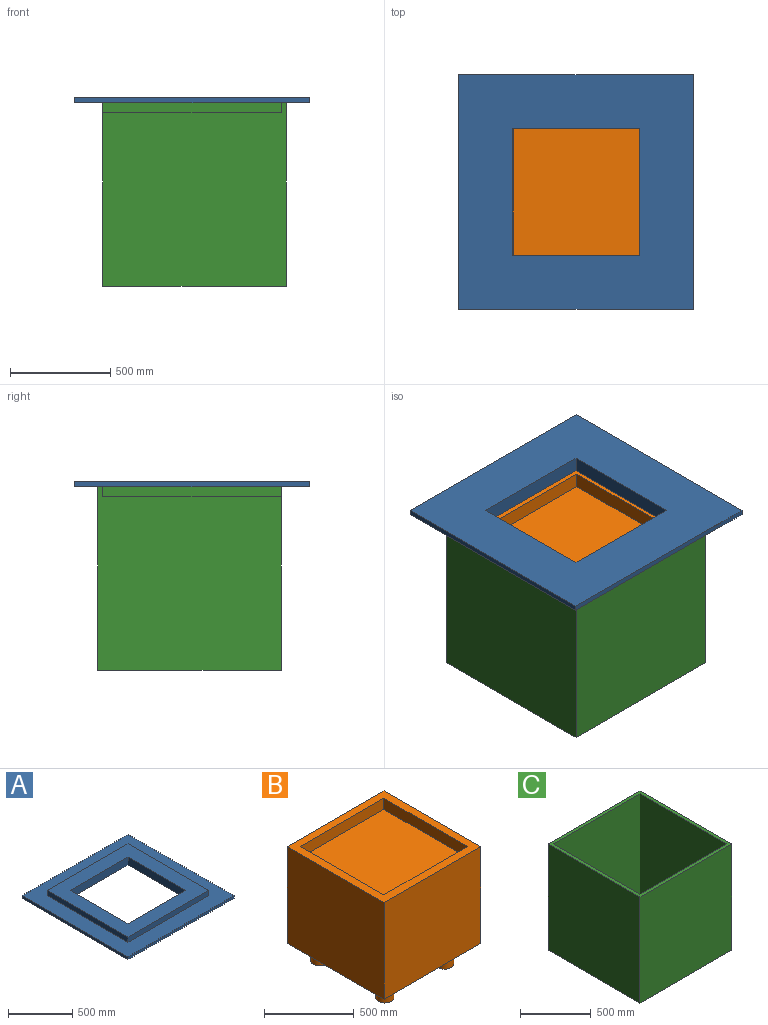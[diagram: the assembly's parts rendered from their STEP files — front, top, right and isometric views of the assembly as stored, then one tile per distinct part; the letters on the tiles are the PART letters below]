
ASSEMBLY  parts=3 mates=2
PART A: 15 faces, bbox 1168.4x1168.4x76.2 mm
  f0: plane 1168.4x1168.4mm, normal (0,0,-1), area 961933.6mm2, adj f3,f4,f5,f6,f11,f12,f13,f14
  f1: plane 889x889mm, normal (0,0,1), area 387096mm2, adj f7,f8,f9,f10,f11,f12,f13,f14
  f2: plane 1168.4x1168.4mm, normal (0,0,1), area 574837.6mm2, adj f3,f4,f5,f6,f7,f8,f9,f10
  f3: plane 1168.4x25.4mm, normal (1,0,0), area 29677.4mm2, adj f0,f2,f4,f6
  f4: plane 1168.4x25.4mm, normal (0,1,0), area 29677.4mm2, adj f0,f2,f3,f5
  f5: plane 1168.4x25.4mm, normal (-1,0,0), area 29677.4mm2, adj f0,f2,f4,f6
  f6: plane 1168.4x25.4mm, normal (0,-1,0), area 29677.4mm2, adj f0,f2,f3,f5
  f7: plane 889x50.8mm, normal (1,0,0), area 45161.2mm2, adj f1,f2,f8,f10
  f8: plane 889x50.8mm, normal (0,1,0), area 45161.2mm2, adj f1,f2,f7,f9
  f9: plane 889x50.8mm, normal (-1,0,0), area 45161.2mm2, adj f1,f2,f8,f10
  f10: plane 889x50.8mm, normal (0,-1,0), area 45161.2mm2, adj f1,f2,f7,f9
  f11: plane 635x76.2mm, normal (0,-1,0), area 48387mm2, adj f0,f1,f12,f13
  f12: plane 635x76.2mm, normal (1,0,0), area 48387mm2, adj f0,f1,f11,f14
  f13: plane 635x76.2mm, normal (-1,0,0), area 48387mm2, adj f0,f1,f11,f14
  f14: plane 635x76.2mm, normal (0,1,0), area 48387mm2, adj f0,f1,f12,f13
PART B: 19 faces, bbox 762x762x787.4 mm
  f0: plane 762x762mm, normal (0,0,1), area 144515.8mm2, adj f1,f2,f3,f4,f6,f7,f8,f9
  f1: plane 762x660.4mm, normal (0,1,0), area 503224.8mm2, adj f0,f2,f4,f5
  f2: plane 762x660.4mm, normal (-1,0,0), area 503224.8mm2, adj f0,f1,f3,f5
  f3: plane 762x660.4mm, normal (0,-1,0), area 503224.8mm2, adj f0,f2,f4,f5
  f4: plane 762x660.4mm, normal (1,0,0), area 503224.8mm2, adj f0,f1,f3,f5
  f5: plane 762x762mm, normal (0,0,-1), area 548214.7mm2, adj f1,f2,f3,f4,f11,f13,f15,f17
  f6: plane 660.4x76.2mm, normal (0,-1,0), area 50322.5mm2, adj f0,f7,f9,f10
  f7: plane 660.4x76.2mm, normal (1,0,0), area 50322.5mm2, adj f0,f6,f8,f10
  f8: plane 660.4x76.2mm, normal (0,1,0), area 50322.5mm2, adj f0,f7,f9,f10
  f9: plane 660.4x76.2mm, normal (-1,0,0), area 50322.5mm2, adj f0,f6,f8,f10
  f10: plane 660.4x660.4mm, normal (0,0,1), area 436128.2mm2, adj f6,f7,f8,f9
  f11: cylinder r=50.8mm len=127mm, axis (0,0,1), area 40536.6mm2, adj f5,f12
  f12: plane 101.6x101.6mm, normal (0,0,-1), area 8107.3mm2, adj f11
  f13: cylinder r=50.8mm len=127mm, axis (0,0,1), area 40536.6mm2, adj f5,f14
  f14: plane 101.6x101.6mm, normal (0,0,-1), area 8107.3mm2, adj f13
  f15: cylinder r=50.8mm len=127mm, axis (0,0,1), area 40536.6mm2, adj f5,f16
  f16: plane 101.6x101.6mm, normal (0,0,-1), area 8107.3mm2, adj f15
  f17: cylinder r=50.8mm len=127mm, axis (0,0,1), area 40536.6mm2, adj f5,f18
  f18: plane 101.6x101.6mm, normal (0,0,-1), area 8107.3mm2, adj f17
PART C: 11 faces, bbox 914.4x914.4x914.4 mm
  f0: plane 914.4x914.4mm, normal (0,0,1), area 90322.4mm2, adj f1,f2,f3,f4,f6,f7,f8,f9
  f1: plane 914.4x914.4mm, normal (0,1,0), area 836127.4mm2, adj f0,f2,f4,f5
  f2: plane 914.4x914.4mm, normal (-1,0,0), area 836127.4mm2, adj f0,f1,f3,f5
  f3: plane 914.4x914.4mm, normal (0,-1,0), area 836127.4mm2, adj f0,f2,f4,f5
  f4: plane 914.4x914.4mm, normal (1,0,0), area 836127.4mm2, adj f0,f1,f3,f5
  f5: plane 914.4x914.4mm, normal (0,0,-1), area 836127.4mm2, adj f1,f2,f3,f4
  f6: plane 889x863.6mm, normal (0,-1,0), area 767740.4mm2, adj f0,f7,f9,f10
  f7: plane 889x863.6mm, normal (1,0,0), area 767740.4mm2, adj f0,f6,f8,f10
  f8: plane 889x863.6mm, normal (0,1,0), area 767740.4mm2, adj f0,f7,f9,f10
  f9: plane 889x863.6mm, normal (-1,0,0), area 767740.4mm2, adj f0,f6,f8,f10
  f10: plane 863.6x863.6mm, normal (0,0,1), area 745805mm2, adj f6,f7,f8,f9
PLACE A rot(axis=(1,0,0),180deg) t=(114.3,73.8,939.8)mm
PLACE B rot(axis=(0,0,1),90deg) t=(-497.3,453.68,152.4)mm
PLACE C t=(-434.49,442.73,0)mm
MATE planar B.f15 <-> C.f10  axis (0,0,-1) through (-715.52,689.43,25.4)mm
MATE fastened A.f2 <-> C.f0  axis (0,0,-1) through (-25.4,889,914.4)mm
